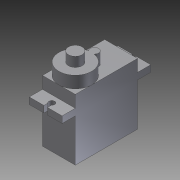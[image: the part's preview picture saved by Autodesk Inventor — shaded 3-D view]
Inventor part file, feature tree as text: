
AUTODESK INVENTOR PART (.ipt)
format: ipt  version: 2011 SP2 (Build 150309200, 309)  size: 144,896 bytes
history: native  units: mm
features: extrude x4, sketch x4, projected_geometry x1
ambient origin geometry x8: Origin, YZ Plane, XZ Plane, XY Plane, X Axis, Y Axis, Z Axis, Center Point
bodies: Solid1 (feature_tree)
feature tree (9):
  extrude  "Extrusion1"  Depth=15.6mm
  extrude  "Extrusion2"  Depth=2.4mm
  extrude  "Extrusion3"  Depth=22.75mm
  extrude  "Extrusion4"  Depth=2.4mm
  sketch  "Sketch1"  dims[d0=11.375mm d1=15.6mm]
  sketch  "Sketch2"  dims[d2=4.825mm d3=2.4mm]
  sketch  "Sketch3"  dims[d4=4.4mm d5=22.75mm]
  sketch  "Sketch4"  dims[d7=4.825mm d8=2.4mm d9=18.0mm d10=12.0mm d11=0.0mm d13=3.0mm d14=4.3mm d15=0.0mm d16=5.0mm d17=3.5mm d18=0.0mm d19=2.1mm d20=2.1mm d21=27.9mm d22=2.25mm d23=1.3mm d25=0.65mm d26=1.3mm d27=0.65mm d28=3.5mm d29=0.0mm]
  projected_geometry  "Projected Loop1"
